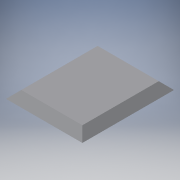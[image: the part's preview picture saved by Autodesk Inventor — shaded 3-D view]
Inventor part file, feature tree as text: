
AUTODESK INVENTOR PART (.ipt)
format: ipt  version: 2016 (Build 200138000, 138)  size: 91,136 bytes
history: native  units: in
note: dims shown in document units (in); Inventor stores cm internally (conversion verified against a paired STEP export)
features: extrude x1, chamfer x1, sketch x1
ambient origin geometry x8: Origin, YZ Plane, XZ Plane, XY Plane, X Axis, Y Axis, Z Axis, Center Point
bodies: Solid1 (feature_tree)
feature tree (3):
  extrude  "Extrusion1"  Depth=2.0in
  chamfer  "Chamfer1"  Distance=2.0in
  sketch  "Sketch1"  dims[d0=24.0in d1=20.0in d2=2.0in d3=0.0in d4=2.0in d5=0.125in d6=45.0deg]
